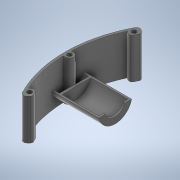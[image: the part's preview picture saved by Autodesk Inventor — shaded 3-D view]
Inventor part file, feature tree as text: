
AUTODESK INVENTOR PART (.ipt)
format: ipt  version: 2020 (Build 240168000, 168)  size: 1,394,688 bytes
history: native  units: mm
features: extrude x17, projected_geometry x13, sketch x8, other x4, fillet x2
ambient origin geometry x8: Origin, YZ Plane, XZ Plane, XY Plane, X Axis, Y Axis, Z Axis, Center Point
bodies: Body1 (feature_tree)
feature tree (44):
  other  "Твердое тело1"
  extrude  "outer"  TaperAngle=45.0deg  [1 undecoded]
  extrude  "inner"  Depth=7.0mm
  extrude  "Выдавливание3"  Depth=20.0mm
  extrude  "Выдавливание4"  Depth=7.0mm
  extrude  "Выдавливание5"  Depth=3.2mm
  extrude  "Выдавливание6"  Depth=59.0mm
  extrude  "Выдавливание7"  Depth=83.0mm
  extrude  "Выдавливание8"  Depth=69.0mm
  sketch  "Эскиз6"
  extrude  "Выдавливание9"  Depth=55.0mm
  extrude  "Выдавливание10"  Depth=3.0mm
  fillet  "Сопряжение1"  Radius=8.0mm
  other  "РабПлоскость2"
  sketch  "Эскиз8"
  extrude  "Выдавливание11"  Depth=5.0mm
  fillet  "Сопряжение2"  Radius=2.0mm
  sketch  "3D эскиз1"
  other  "РабПлоскость4"
  sketch  "Эскиз11"
  extrude  "Выдавливание12"  Depth=40.0mm TaperAngle=360.0deg
  extrude  "Выдавливание13"  Depth=2.0mm
  extrude  "Выдавливание14"  Depth=105.0mm
  extrude  "Выдавливание15"  Depth=2.0mm
  extrude  "Выдавливание16"  Depth=2.0mm TaperAngle=0.0deg
  extrude  "Выдавливание17"  Depth=3.5mm
  sketch  "Эскиз1"
  sketch  "Эскиз2"
  projected_geometry  "Спроецированная петля1"
  projected_geometry  "Спроецированная петля2"
  projected_geometry  "Спроецированная петля3"
  projected_geometry  "Спроецированная петля4"
  projected_geometry  "Спроецированная петля5"
  projected_geometry  "Спроецированная петля8"
  projected_geometry  "Спроецированная петля9"
  projected_geometry  "Спроецированная петля10"
  other  "Проецирование на поверхность1"
  projected_geometry  "Спроецированная петля14"
  projected_geometry  "Спроецированная петля15"
  projected_geometry  "Спроецированная петля16"
  sketch  "Эскиз12"
  projected_geometry  "Спроецированная петля17"
  sketch  "Эскиз13"
  projected_geometry  "Спроецированная петля18"
note: 1 required parameter value undecoded (feature->parameter linkage not recoverable at this tier; creation-order binding heuristic only, values carry confidence <= 0.55)
